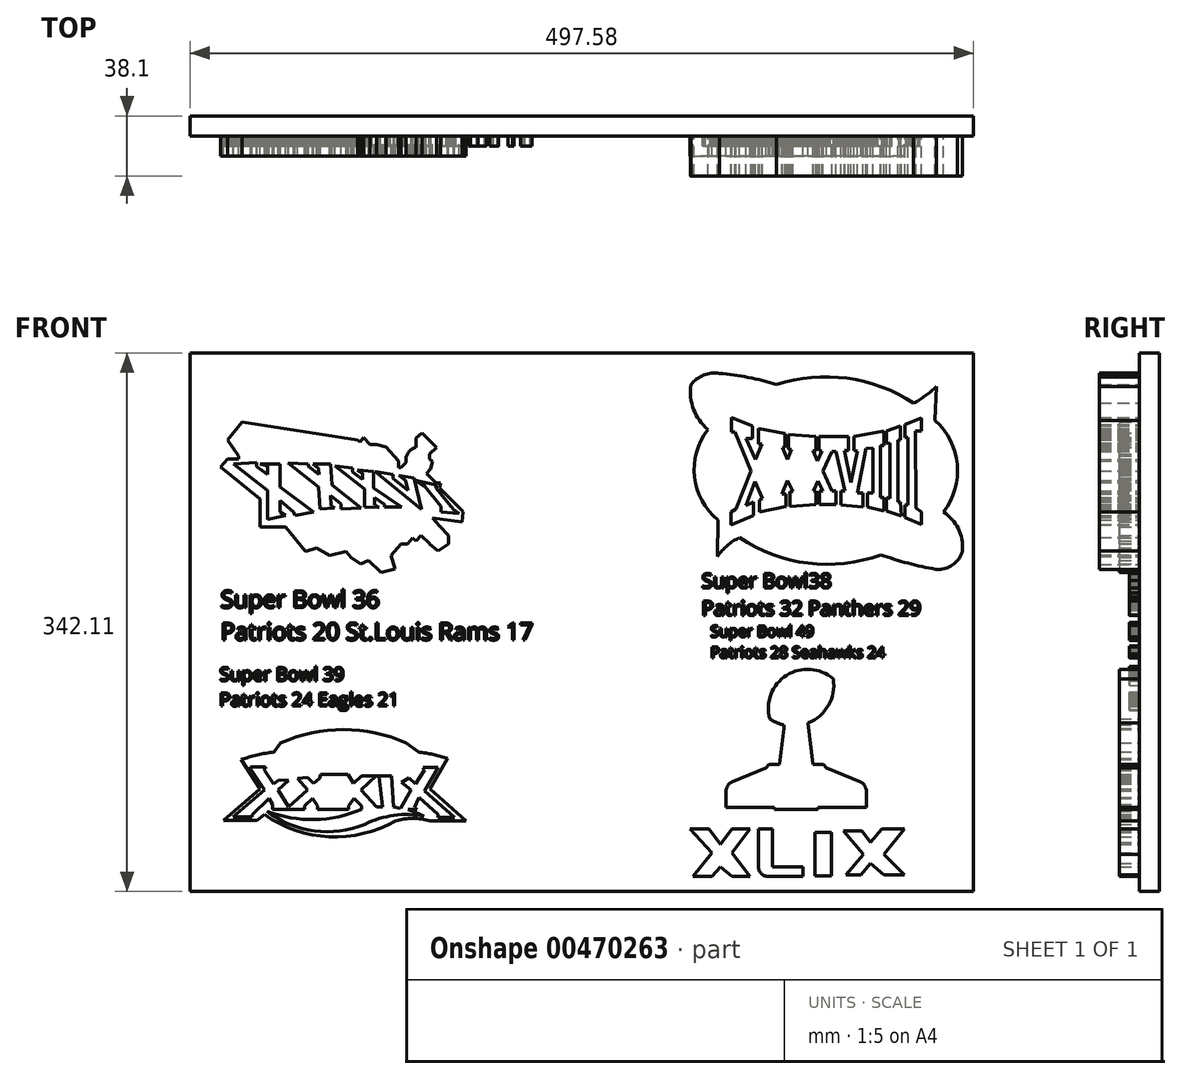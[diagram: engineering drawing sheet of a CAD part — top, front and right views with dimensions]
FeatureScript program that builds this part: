
annotation { "Feature Type Name" : "Feature", "Feature Type Description" : "" }
export const myFeature = defineFeature(function(context is Context, id is Id, definition is map)
    precondition{}
    {
        {
            var Q0;
            Q0=qCreatedBy(makeId("Front.planeOp"),FACE);
            var sketch = newSketch(context, id + "F0", { "sketchPlane" : qUnion([Q0])});
            skLineSegment(sketch, "E0.bottom", {"start": v(-44.55, 100.86) * mm, "end": v(453.03, 100.86) * mm});
            skLineSegment(sketch, "E0.top", {"start": v(-44.55, -241.25) * mm, "end": v(453.03, -241.25) * mm});
            skLineSegment(sketch, "E0.left", {"start": v(-44.55, 100.86) * mm, "end": v(-44.55, -241.25) * mm});
            skLineSegment(sketch, "E0.right", {"start": v(453.03, 100.86) * mm, "end": v(453.03, -241.25) * mm});
            skSolve(sketch);
        }
        {
            var Q0;
            Q0 = qSketchRegion(id + "F0", true);
            extrude(context, id + "F1", {"entities" : qUnion([Q0]), "depth" : 12.7 * mm});
        }
        {
            var Q0;
            Q0=makeQuery(id+"F1.opExtrude","CAP_FACE",FACE,{"disambiguationData":[OSD([sQuery(id+"F0.wireOp",EDGE,"E0.bottom"),sQuery(id+"F0.wireOp",EDGE,"E0.top"),sQuery(id+"F0.wireOp",EDGE,"E0.left"),sQuery(id+"F0.wireOp",EDGE,"E0.right")])],"isStart":false});
            var sketch = newSketch(context, id + "F2", { "sketchPlane" : qUnion([Q0])});
            skArc(sketch, "E1", {"start": v(289.89, 58.13) * mm, "mid": v(275.62, 26.24) * mm, "end": v(290.82, -5.22) * mm});
            skArc(sketch, "E2", {"start": v(415.04, 68.98) * mm, "mid": v(350.57, 85.37) * mm, "end": v(289.89, 58.13) * mm});
            skArc(sketch, "E3", {"start": v(428.71, -5.7) * mm, "mid": v(442.95, 26.22) * mm, "end": v(428.71, 58.13) * mm});
            skArc(sketch, "E4", {"start": v(304.5, -16.36) * mm, "mid": v(368.5, -33) * mm, "end": v(428.71, -5.7) * mm});
            skArc(sketch, "E5", {"start": v(304.5, -16.36) * mm, "mid": v(296.68, -21.46) * mm, "end": v(290.46, -28.4) * mm});
            skArc(sketch, "E6", {"start": v(415.04, 68.98) * mm, "mid": v(422.63, 73.85) * mm, "end": v(429.6, 79.58) * mm});
            skLineSegment(sketch, "E7", {"start": v(429.6, 79.58) * mm, "end": v(428.71, 58.13) * mm});
            skLineSegment(sketch, "E8", {"start": v(290.82, -5.22) * mm, "end": v(290.46, -28.4) * mm});
            skArc(sketch, "E9", {"start": v(273.65, 80.73) * mm, "mid": v(275.27, 65.1) * mm, "end": v(284.32, 52.25) * mm});
            skArc(sketch, "E10", {"start": v(291.58, 87.97) * mm, "mid": v(281.63, 86.8) * mm, "end": v(273.65, 80.73) * mm});
            skArc(sketch, "E11", {"start": v(327.86, 80.73) * mm, "mid": v(309.93, 85.41) * mm, "end": v(291.58, 87.97) * mm});
            skArc(sketch, "E12", {"start": v(446.06, -24.78) * mm, "mid": v(443.4, -10.76) * mm, "end": v(434, 0) * mm});
            skArc(sketch, "E13", {"start": v(429.16, -36.5) * mm, "mid": v(439.76, -33.75) * mm, "end": v(446.06, -24.78) * mm});
            skArc(sketch, "E14", {"start": v(394.14, -27.3) * mm, "mid": v(411.45, -32.67) * mm, "end": v(429.16, -36.5) * mm});
            skLineSegment(sketch, "E15", {"start": v(299.48, 59.78) * mm, "end": v(299.48, 50.73) * mm});
            skLineSegment(sketch, "E16", {"start": v(299.48, 50.73) * mm, "end": v(301.47, 50.73) * mm});
            skLineSegment(sketch, "E17", {"start": v(301.47, 50.73) * mm, "end": v(311.84, 26) * mm});
            skLineSegment(sketch, "E18", {"start": v(311.84, 26) * mm, "end": v(302.35, 1.93) * mm});
            skLineSegment(sketch, "E19", {"start": v(302.35, 1.93) * mm, "end": v(299.04, 0) * mm});
            skLineSegment(sketch, "E20", {"start": v(299.04, 0) * mm, "end": v(299.04, -8.45) * mm});
            skLineSegment(sketch, "E21", {"start": v(299.04, -8.45) * mm, "end": v(313.39, -2.49) * mm});
            skLineSegment(sketch, "E22", {"start": v(313.39, -2.49) * mm, "end": v(313.39, 6.12) * mm});
            skLineSegment(sketch, "E23", {"start": v(313.39, 6.12) * mm, "end": v(308.53, 4.14) * mm});
            skLineSegment(sketch, "E24", {"start": v(308.53, 4.14) * mm, "end": v(314.27, 19.15) * mm});
            skLineSegment(sketch, "E25", {"start": v(314.27, 19.15) * mm, "end": v(318.9, 8.33) * mm});
            skLineSegment(sketch, "E26", {"start": v(318.9, 8.33) * mm, "end": v(317.04, 7.53) * mm});
            skLineSegment(sketch, "E27", {"start": v(317.04, 7.53) * mm, "end": v(317.04, 0) * mm});
            skLineSegment(sketch, "E28", {"start": v(317.04, 0) * mm, "end": v(333.85, 3.41) * mm});
            skLineSegment(sketch, "E29", {"start": v(333.85, 3.41) * mm, "end": v(333.85, 11.28) * mm});
            skLineSegment(sketch, "E30", {"start": v(333.85, 11.28) * mm, "end": v(331.34, 11.28) * mm});
            skLineSegment(sketch, "E31", {"start": v(331.34, 11.28) * mm, "end": v(335.03, 19.99) * mm});
            skLineSegment(sketch, "E32", {"start": v(335.03, 19.99) * mm, "end": v(338.54, 12.79) * mm});
            skLineSegment(sketch, "E33", {"start": v(338.54, 12.79) * mm, "end": v(336.36, 12.79) * mm});
            skLineSegment(sketch, "E34", {"start": v(336.36, 12.79) * mm, "end": v(336.36, 3.41) * mm});
            skLineSegment(sketch, "E35", {"start": v(336.36, 3.41) * mm, "end": v(353.1, 4.75) * mm});
            skLineSegment(sketch, "E36", {"start": v(317.04, 26.85) * mm, "end": v(324.14, 9.14) * mm});
            skLineSegment(sketch, "E37", {"start": v(317.04, 26.85) * mm, "end": v(324.14, 41.96) * mm});
            skLineSegment(sketch, "E38", {"start": v(324.14, 41.96) * mm, "end": v(325.9, 41.96) * mm});
            skLineSegment(sketch, "E39", {"start": v(325.9, 41.96) * mm, "end": v(332.27, 26.45) * mm});
            skLineSegment(sketch, "E40", {"start": v(332.27, 26.45) * mm, "end": v(325.9, 9.57) * mm});
            skLineSegment(sketch, "E41", {"start": v(324.14, 9.14) * mm, "end": v(325.9, 9.57) * mm});
            skLineSegment(sketch, "E42", {"start": v(318.57, 43.21) * mm, "end": v(314.54, 33.27) * mm});
            skLineSegment(sketch, "E43", {"start": v(318.57, 43.21) * mm, "end": v(316.5, 43.21) * mm});
            skLineSegment(sketch, "E44", {"start": v(316.5, 43.21) * mm, "end": v(316.5, 53.05) * mm});
            skLineSegment(sketch, "E45", {"start": v(314.54, 33.27) * mm, "end": v(308.63, 46.63) * mm});
            skLineSegment(sketch, "E46", {"start": v(308.63, 46.63) * mm, "end": v(312.57, 46.63) * mm});
            skLineSegment(sketch, "E47", {"start": v(312.57, 46.63) * mm, "end": v(312.57, 54.6) * mm});
            skLineSegment(sketch, "E48", {"start": v(312.57, 54.6) * mm, "end": v(299.48, 59.78) * mm});
            skLineSegment(sketch, "E49", {"start": v(316.5, 53.05) * mm, "end": v(333.42, 49.68) * mm});
            skLineSegment(sketch, "E50", {"start": v(333.42, 49.68) * mm, "end": v(333.42, 40.97) * mm});
            skLineSegment(sketch, "E51", {"start": v(333.42, 40.97) * mm, "end": v(331.8, 40.97) * mm});
            skLineSegment(sketch, "E52", {"start": v(331.8, 40.97) * mm, "end": v(335.02, 33.27) * mm});
            skLineSegment(sketch, "E53", {"start": v(335.02, 33.27) * mm, "end": v(337.53, 39.44) * mm});
            skLineSegment(sketch, "E54", {"start": v(337.53, 39.44) * mm, "end": v(335.64, 39.44) * mm});
            skLineSegment(sketch, "E55", {"start": v(335.64, 39.44) * mm, "end": v(335.64, 49.17) * mm});
            skLineSegment(sketch, "E56", {"start": v(335.64, 49.17) * mm, "end": v(353.02, 47.75) * mm});
            skLineSegment(sketch, "E57", {"start": v(353.1, 4.75) * mm, "end": v(353.1, 13.17) * mm});
            skLineSegment(sketch, "E58", {"start": v(353.1, 13.17) * mm, "end": v(351.4, 13.17) * mm});
            skLineSegment(sketch, "E59", {"start": v(351.4, 13.17) * mm, "end": v(354.26, 19.44) * mm});
            skLineSegment(sketch, "E60", {"start": v(354.26, 19.44) * mm, "end": v(357.44, 13.17) * mm});
            skLineSegment(sketch, "E61", {"start": v(357.44, 13.17) * mm, "end": v(355.27, 13.17) * mm});
            skLineSegment(sketch, "E62", {"start": v(355.27, 13.17) * mm, "end": v(355.27, 4.75) * mm});
            skLineSegment(sketch, "E63", {"start": v(355.27, 4.75) * mm, "end": v(365.63, 4.75) * mm});
            skLineSegment(sketch, "E64", {"start": v(365.63, 4.66) * mm, "end": v(365.63, 13.17) * mm});
            skLineSegment(sketch, "E65", {"start": v(365.63, 13.17) * mm, "end": v(363.08, 13.17) * mm});
            skLineSegment(sketch, "E66", {"start": v(363.08, 13.17) * mm, "end": v(357.44, 25.8) * mm});
            skLineSegment(sketch, "E67", {"start": v(357.44, 25.8) * mm, "end": v(363.08, 38.15) * mm});
            skLineSegment(sketch, "E68", {"start": v(363.08, 38.15) * mm, "end": v(365.63, 38.15) * mm});
            skLineSegment(sketch, "E69", {"start": v(353.02, 47.75) * mm, "end": v(353.02, 38.63) * mm});
            skLineSegment(sketch, "E70", {"start": v(353.02, 38.63) * mm, "end": v(351.08, 38.79) * mm});
            skLineSegment(sketch, "E71", {"start": v(351.08, 38.79) * mm, "end": v(353.88, 32.1) * mm});
            skLineSegment(sketch, "E72", {"start": v(353.88, 32.1) * mm, "end": v(356.95, 38.63) * mm});
            skLineSegment(sketch, "E73", {"start": v(356.95, 38.63) * mm, "end": v(355.01, 38.79) * mm});
            skLineSegment(sketch, "E74", {"start": v(355.01, 38.79) * mm, "end": v(355.01, 47.75) * mm});
            skLineSegment(sketch, "E75", {"start": v(356.95, 47.75) * mm, "end": v(373.54, 47.75) * mm});
            skLineSegment(sketch, "E76", {"start": v(373.54, 47.75) * mm, "end": v(373.54, 38.79) * mm});
            skLineSegment(sketch, "E77", {"start": v(373.54, 38.79) * mm, "end": v(371.1, 38.99) * mm});
            skLineSegment(sketch, "E78", {"start": v(371.1, 38.99) * mm, "end": v(375.28, 18.71) * mm});
            skLineSegment(sketch, "E79", {"start": v(375.28, 18.71) * mm, "end": v(379.2, 38.63) * mm});
            skLineSegment(sketch, "E80", {"start": v(379.2, 38.63) * mm, "end": v(377.27, 38.79) * mm});
            skLineSegment(sketch, "E81", {"start": v(377.27, 38.79) * mm, "end": v(377.27, 47.75) * mm});
            skLineSegment(sketch, "E82", {"start": v(355.01, 47.75) * mm, "end": v(356.95, 47.75) * mm});
            skLineSegment(sketch, "E83", {"start": v(343.5, 12.78) * mm, "end": v(346.08, 12.78) * mm});
            skLineSegment(sketch, "E84", {"start": v(346.08, 12.78) * mm, "end": v(352.05, 25.84) * mm});
            skLineSegment(sketch, "E85", {"start": v(352.05, 25.84) * mm, "end": v(346.08, 38.7) * mm});
            skLineSegment(sketch, "E86", {"start": v(346.08, 38.7) * mm, "end": v(343.38, 38.7) * mm});
            skLineSegment(sketch, "E87", {"start": v(343.38, 38.7) * mm, "end": v(337.5, 25.84) * mm});
            skLineSegment(sketch, "E88", {"start": v(337.5, 25.84) * mm, "end": v(343.5, 12.78) * mm});
            skLineSegment(sketch, "E89", {"start": v(365.63, 38.15) * mm, "end": v(371.36, 13.21) * mm});
            skLineSegment(sketch, "E90", {"start": v(371.36, 13.21) * mm, "end": v(368.86, 13.21) * mm});
            skLineSegment(sketch, "E91", {"start": v(368.86, 13.21) * mm, "end": v(368.86, 4.17) * mm});
            skLineSegment(sketch, "E92", {"start": v(368.86, 4.17) * mm, "end": v(382.76, 3.06) * mm});
            skLineSegment(sketch, "E93", {"start": v(382.76, 3.06) * mm, "end": v(382.76, 11.82) * mm});
            skLineSegment(sketch, "E94", {"start": v(382.76, 11.82) * mm, "end": v(379.43, 11.82) * mm});
            skLineSegment(sketch, "E95", {"start": v(379.43, 11.82) * mm, "end": v(384.71, 40.06) * mm});
            skLineSegment(sketch, "E96", {"start": v(384.71, 40.06) * mm, "end": v(389.16, 40.47) * mm});
            skLineSegment(sketch, "E97", {"start": v(389.16, 40.47) * mm, "end": v(389.16, 11.82) * mm});
            skLineSegment(sketch, "E98", {"start": v(389.16, 11.82) * mm, "end": v(385.69, 11.82) * mm});
            skLineSegment(sketch, "E99", {"start": v(385.69, 11.82) * mm, "end": v(385.69, 3.06) * mm});
            skLineSegment(sketch, "E100", {"start": v(385.69, 3.06) * mm, "end": v(396.26, 0.42) * mm});
            skLineSegment(sketch, "E101", {"start": v(396.26, 0.42) * mm, "end": v(396.26, 9.04) * mm});
            skLineSegment(sketch, "E102", {"start": v(396.26, 9.04) * mm, "end": v(394.03, 9.04) * mm});
            skLineSegment(sketch, "E103", {"start": v(394.03, 9.04) * mm, "end": v(394.03, 42) * mm});
            skLineSegment(sketch, "E104", {"start": v(394.03, 42) * mm, "end": v(396.12, 42) * mm});
            skLineSegment(sketch, "E105", {"start": v(396.12, 42) * mm, "end": v(396.12, 51.46) * mm});
            skLineSegment(sketch, "E106", {"start": v(396.12, 51.46) * mm, "end": v(377.27, 47.75) * mm});
            skLineSegment(sketch, "E107", {"start": v(397.84, 51.46) * mm, "end": v(397.84, 43.46) * mm});
            skLineSegment(sketch, "E108", {"start": v(397.84, 43.46) * mm, "end": v(399.89, 43.65) * mm});
            skLineSegment(sketch, "E109", {"start": v(399.89, 43.65) * mm, "end": v(399.89, 8.6) * mm});
            skLineSegment(sketch, "E110", {"start": v(399.89, 8.6) * mm, "end": v(397.84, 9.04) * mm});
            skLineSegment(sketch, "E111", {"start": v(397.84, 9.04) * mm, "end": v(397.84, 0.42) * mm});
            skLineSegment(sketch, "E112", {"start": v(397.84, 0.42) * mm, "end": v(407.35, -2.58) * mm});
            skLineSegment(sketch, "E113", {"start": v(407.35, -2.58) * mm, "end": v(406.51, 6.3) * mm});
            skLineSegment(sketch, "E114", {"start": v(406.51, 6.3) * mm, "end": v(405, 6.15) * mm});
            skLineSegment(sketch, "E115", {"start": v(405, 6.15) * mm, "end": v(405, 45.5) * mm});
            skLineSegment(sketch, "E116", {"start": v(405, 45.5) * mm, "end": v(406.51, 45.65) * mm});
            skLineSegment(sketch, "E117", {"start": v(406.51, 45.65) * mm, "end": v(406.51, 54.6) * mm});
            skLineSegment(sketch, "E118", {"start": v(406.51, 54.6) * mm, "end": v(397.84, 51.46) * mm});
            skLineSegment(sketch, "E119", {"start": v(409.62, 47.3) * mm, "end": v(409.62, 55.37) * mm});
            skLineSegment(sketch, "E120", {"start": v(409.62, 47.3) * mm, "end": v(411.5, 47.3) * mm});
            skLineSegment(sketch, "E121", {"start": v(411.5, 47.3) * mm, "end": v(411.5, 4.35) * mm});
            skLineSegment(sketch, "E122", {"start": v(411.5, 4.35) * mm, "end": v(409.62, 4.35) * mm});
            skLineSegment(sketch, "E123", {"start": v(409.62, 4.35) * mm, "end": v(409.62, -3.56) * mm});
            skLineSegment(sketch, "E124", {"start": v(409.62, -3.56) * mm, "end": v(420, -7.9) * mm});
            skLineSegment(sketch, "E125", {"start": v(420, -7.9) * mm, "end": v(420, 0) * mm});
            skLineSegment(sketch, "E126", {"start": v(420, 0) * mm, "end": v(416.46, 2.38) * mm});
            skLineSegment(sketch, "E127", {"start": v(416.06, 51.33) * mm, "end": v(416.46, 2.38) * mm});
            skPoint(sketch, "E127.startSnap0", {"position": v(409.62, 51.33) * mm});
            skLineSegment(sketch, "E128", {"start": v(416.06, 51.33) * mm, "end": v(420, 51.37) * mm});
            skLineSegment(sketch, "E129", {"start": v(420, 51.37) * mm, "end": v(419.92, 59.7) * mm});
            skLineSegment(sketch, "E130", {"start": v(419.92, 59.7) * mm, "end": v(409.62, 55.37) * mm});
            skSolve(sketch);
        }
        {
            var Q0;
            Q0 = qSketchRegion(id + "F2", true);
            extrude(context, id + "F3", {"entities" : qUnion([Q0]), "operationType" : NewBodyOperationType.ADD, "depth" : 25.4 * mm});
        }
        {
            var Q0;
            {var subQ0=sQuery(id+"F0.wireOp",EDGE,"E0.left");var subQ1=sQuery(id+"F0.wireOp",EDGE,"E0.bottom");var subQ2=sQuery(id+"F0.wireOp",EDGE,"E0.right");var subQ3=sQuery(id+"F0.wireOp",EDGE,"E0.top");Q0=makeQuery(id+"F3.boolean.opBoolean","SPLIT",FACE,{"disambiguationData":[TD([makeQuery(id+"F1.opExtrude","SWEPT_FACE",FACE,{"disambiguationData":[OSD([subQ1])]})])],"derivedFrom":makeQuery(id+"F1.opExtrude","CAP_FACE",FACE,{"disambiguationData":[OSD([subQ1,subQ3,subQ0,subQ2])],"isStart":false})});}
            var sketch = newSketch(context, id + "F4", { "sketchPlane" : qUnion([Q0])});
            skLineSegment(sketch, "E131", {"start": v(326.56, -189.04) * mm, "end": v(347.97, -189.04) * mm});
            skLineSegment(sketch, "E132", {"start": v(347.97, -189.04) * mm, "end": v(344.69, -135.26) * mm});
            skLineSegment(sketch, "E133", {"start": v(348.03, -134.17) * mm, "end": v(354.36, -189.04) * mm});
            skLineSegment(sketch, "E134", {"start": v(354.36, -189.04) * mm, "end": v(347.97, -189.04) * mm});
            skLineSegment(sketch, "E135", {"start": v(326.56, -189.04) * mm, "end": v(332.51, -137.46) * mm});
            skPoint(sketch, "E136.orphan", {"position": v(344.6, -133.69) * mm});
            skArc(sketch, "E137", {"start": v(363.98, -106.14) * mm, "mid": v(334.37, -103.83) * mm, "end": v(323.67, -131.54) * mm});
            skArc(sketch, "E138", {"start": v(323.67, -131.54) * mm, "mid": v(352.16, -132.06) * mm, "end": v(363.98, -106.14) * mm});
            skLineSegment(sketch, "E139", {"start": v(332.51, -137.46) * mm, "end": v(332.51, -135.4) * mm});
            skPoint(sketch, "E140.orphan", {"position": v(347.97, -133.69) * mm});
            skLineSegment(sketch, "E141", {"start": v(272.83, -201.33) * mm, "end": v(284.99, -201.33) * mm});
            skLineSegment(sketch, "E142", {"start": v(284.99, -201.33) * mm, "end": v(292.35, -211.27) * mm});
            skLineSegment(sketch, "E143", {"start": v(292.35, -211.27) * mm, "end": v(299.72, -201.33) * mm});
            skLineSegment(sketch, "E144", {"start": v(299.72, -201.33) * mm, "end": v(311.14, -201.33) * mm});
            skLineSegment(sketch, "E145", {"start": v(311.14, -201.33) * mm, "end": v(299.72, -216.8) * mm});
            skLineSegment(sketch, "E146", {"start": v(299.72, -216.8) * mm, "end": v(311.14, -231.66) * mm});
            skLineSegment(sketch, "E147", {"start": v(311.14, -231.66) * mm, "end": v(299.72, -231.66) * mm});
            skLineSegment(sketch, "E148", {"start": v(299.72, -231.66) * mm, "end": v(292.35, -225.4) * mm});
            skLineSegment(sketch, "E149", {"start": v(292.35, -225.4) * mm, "end": v(287.03, -231.66) * mm});
            skLineSegment(sketch, "E150", {"start": v(287.03, -231.66) * mm, "end": v(275, -231.66) * mm});
            skLineSegment(sketch, "E151", {"start": v(275, -231.66) * mm, "end": v(287.03, -216.8) * mm});
            skLineSegment(sketch, "E152", {"start": v(287.03, -216.8) * mm, "end": v(272.83, -201.33) * mm});
            skLineSegment(sketch, "E153", {"start": v(316.45, -201.33) * mm, "end": v(316.45, -225.3) * mm});
            skLineSegment(sketch, "E154", {"start": v(322.8, -231.66) * mm, "end": v(344.65, -231.66) * mm});
            skLineSegment(sketch, "E155", {"start": v(344.65, -231.66) * mm, "end": v(344.65, -225.4) * mm});
            skLineSegment(sketch, "E156", {"start": v(344.65, -225.4) * mm, "end": v(325.5, -225.4) * mm});
            skLineSegment(sketch, "E157", {"start": v(325.5, -225.4) * mm, "end": v(325.5, -201.33) * mm});
            skLineSegment(sketch, "E158", {"start": v(325.5, -201.33) * mm, "end": v(316.45, -201.33) * mm});
            skLineSegment(sketch, "E159.bottom", {"start": v(352.39, -203.54) * mm, "end": v(362.7, -203.54) * mm});
            skLineSegment(sketch, "E159.top", {"start": v(352.39, -231.16) * mm, "end": v(362.7, -231.16) * mm});
            skLineSegment(sketch, "E159.left", {"start": v(352.39, -203.54) * mm, "end": v(352.39, -231.16) * mm});
            skLineSegment(sketch, "E159.right", {"start": v(362.7, -203.54) * mm, "end": v(362.7, -231.16) * mm});
            skPoint(sketch, "E160.visualSharp", {"position": v(316.45, -231.66) * mm});
            skArc(sketch, "E160.filletArc", {"start": v(316.45, -225.3) * mm, "mid": v(318.31, -229.8) * mm, "end": v(322.8, -231.66) * mm});
            skLineSegment(sketch, "E161", {"start": v(370.43, -202.54) * mm, "end": v(382.27, -202.54) * mm});
            skLineSegment(sketch, "E162", {"start": v(394.96, -201.47) * mm, "end": v(409.26, -201.47) * mm});
            skLineSegment(sketch, "E163", {"start": v(409.26, -201.47) * mm, "end": v(396.24, -217.45) * mm});
            skLineSegment(sketch, "E164", {"start": v(396.24, -217.45) * mm, "end": v(409.26, -230.48) * mm});
            skLineSegment(sketch, "E165", {"start": v(409.26, -230.48) * mm, "end": v(396.24, -230.48) * mm});
            skLineSegment(sketch, "E166", {"start": v(396.24, -230.48) * mm, "end": v(387.62, -223.25) * mm});
            skLineSegment(sketch, "E167", {"start": v(387.62, -223.25) * mm, "end": v(381.56, -230.48) * mm});
            skLineSegment(sketch, "E168", {"start": v(381.56, -230.48) * mm, "end": v(372.09, -230.48) * mm});
            skLineSegment(sketch, "E169", {"start": v(372.09, -230.48) * mm, "end": v(383.22, -217.45) * mm});
            skLineSegment(sketch, "E170", {"start": v(383.22, -217.45) * mm, "end": v(370.43, -202.54) * mm});
            skLineSegment(sketch, "E171", {"start": v(382.27, -202.54) * mm, "end": v(387.62, -209.99) * mm});
            skLineSegment(sketch, "E172", {"start": v(387.62, -209.99) * mm, "end": v(394.96, -201.47) * mm});
            skLineSegment(sketch, "E173", {"start": v(295.92, -187.74) * mm, "end": v(295.92, -177.52) * mm});
            skLineSegment(sketch, "E174", {"start": v(299.8, -171.67) * mm, "end": v(321.26, -162.66) * mm});
            skLineSegment(sketch, "E175", {"start": v(321.26, -162.66) * mm, "end": v(323.03, -160.38) * mm});
            skLineSegment(sketch, "E176", {"start": v(323.03, -160.38) * mm, "end": v(329.87, -160.38) * mm});
            skLineSegment(sketch, "E177", {"start": v(295.92, -187.74) * mm, "end": v(326.7, -187.74) * mm});
            skPoint(sketch, "E178.visualSharp", {"position": v(295.92, -173.3) * mm});
            skArc(sketch, "E178.filletArc", {"start": v(299.8, -171.67) * mm, "mid": v(296.98, -174) * mm, "end": v(295.92, -177.52) * mm});
            skLineSegment(sketch, "E179", {"start": v(340.46, -189.04) * mm, "end": v(340.46, -130.63) * mm, "construction": true});
            skLineSegment(sketch, "E180.MirrorCS", {"start": v(357.9, -160.38) * mm, "end": v(351.05, -160.38) * mm});
            skLineSegment(sketch, "E181.MirrorCS", {"start": v(381.11, -171.67) * mm, "end": v(359.67, -162.66) * mm});
            skLineSegment(sketch, "E182.MirrorCS", {"start": v(359.67, -162.66) * mm, "end": v(357.9, -160.38) * mm});
            skArc(sketch, "E183.MirrorCS", {"start": v(381.11, -171.67) * mm, "mid": v(383.94, -174) * mm, "end": v(385, -177.52) * mm});
            skLineSegment(sketch, "E184.MirrorCS", {"start": v(385, -187.74) * mm, "end": v(385, -177.52) * mm});
            skLineSegment(sketch, "E185.MirrorCS", {"start": v(385, -187.74) * mm, "end": v(354.21, -187.74) * mm});
            skSolve(sketch);
        }
        {
            var Q0;
            Q0 = qSketchRegion(id + "F4", true);
            extrude(context, id + "F5", {"entities" : qUnion([Q0]), "operationType" : NewBodyOperationType.ADD, "depth" : 12.7 * mm});
        }
        {
            var Q0;
            {var subQ0=sQuery(id+"F0.wireOp",EDGE,"E0.left");var subQ1=sQuery(id+"F0.wireOp",EDGE,"E0.bottom");var subQ2=sQuery(id+"F0.wireOp",EDGE,"E0.right");var subQ3=sQuery(id+"F0.wireOp",EDGE,"E0.top");Q0=makeQuery(id+"F3.boolean.opBoolean","SPLIT",FACE,{"disambiguationData":[TD([makeQuery(id+"F1.opExtrude","SWEPT_FACE",FACE,{"disambiguationData":[OSD([subQ1])]})])],"derivedFrom":makeQuery(id+"F1.opExtrude","CAP_FACE",FACE,{"disambiguationData":[OSD([subQ1,subQ3,subQ0,subQ2])],"isStart":false})});}
            var sketch = newSketch(context, id + "F6", { "sketchPlane" : qUnion([Q0])});
            skLineSegment(sketch, "E186", {"start": v(8.94, -152.54) * mm, "end": v(13.1, -146.72) * mm});
            skLineSegment(sketch, "E187", {"start": v(92.67, -146.72) * mm, "end": v(100.5, -152.54) * mm});
            skArc(sketch, "E188", {"start": v(92.67, -146.72) * mm, "mid": v(52.88, -138.38) * mm, "end": v(13.1, -146.72) * mm});
            skArc(sketch, "E189", {"start": v(8.94, -152.54) * mm, "mid": v(-1.74, -154.47) * mm, "end": v(-12.18, -157.42) * mm});
            skArc(sketch, "E190.MirrorCS", {"start": v(100.5, -152.54) * mm, "mid": v(109.85, -154.18) * mm, "end": v(119.03, -156.6) * mm});
            skLineSegment(sketch, "E191", {"start": v(119.03, -156.6) * mm, "end": v(107.85, -175.9) * mm});
            skLineSegment(sketch, "E192", {"start": v(107.85, -175.9) * mm, "end": v(130.84, -196.28) * mm});
            skLineSegment(sketch, "E193", {"start": v(130.84, -196.28) * mm, "end": v(107.85, -196.28) * mm});
            skArc(sketch, "E194", {"start": v(107.85, -196.28) * mm, "mid": v(97, -194.75) * mm, "end": v(86.15, -196.28) * mm});
            skArc(sketch, "E195", {"start": v(2.65, -192.28) * mm, "mid": v(43.82, -206.36) * mm, "end": v(86.15, -196.28) * mm});
            skLineSegment(sketch, "E196", {"start": v(-12.18, -157.42) * mm, "end": v(0, -175.95) * mm});
            skLineSegment(sketch, "E197", {"start": v(0, -175.95) * mm, "end": v(-23.3, -196.17) * mm});
            skLineSegment(sketch, "E198", {"start": v(-23.3, -196.17) * mm, "end": v(-1.96, -196.17) * mm});
            skLineSegment(sketch, "E199", {"start": v(-1.96, -196.17) * mm, "end": v(2.65, -192.28) * mm});
            skLineSegment(sketch, "E200", {"start": v(-6.09, -163.29) * mm, "end": v(2.65, -176.58) * mm});
            skPoint(sketch, "E200.startSnap0", {"position": v(-6.09, -166.69) * mm});
            skLineSegment(sketch, "E201", {"start": v(2.65, -176.58) * mm, "end": v(-17.17, -193.78) * mm});
            skLineSegment(sketch, "E202", {"start": v(-17.17, -193.78) * mm, "end": v(-5.3, -193.78) * mm});
            skLineSegment(sketch, "E203", {"start": v(-5.3, -193.78) * mm, "end": v(-5.3, -192.55) * mm});
            skLineSegment(sketch, "E204", {"start": v(-5.3, -192.55) * mm, "end": v(5.77, -182.03) * mm});
            skLineSegment(sketch, "E205", {"start": v(5.77, -182.03) * mm, "end": v(7.94, -185.8) * mm});
            skLineSegment(sketch, "E206", {"start": v(7.94, -185.8) * mm, "end": v(7.94, -189) * mm});
            skLineSegment(sketch, "E207", {"start": v(7.94, -189) * mm, "end": v(28.06, -189) * mm});
            skLineSegment(sketch, "E208", {"start": v(28.06, -189) * mm, "end": v(28.06, -186.83) * mm});
            skLineSegment(sketch, "E209", {"start": v(28.06, -186.83) * mm, "end": v(33.21, -182.03) * mm});
            skLineSegment(sketch, "E210", {"start": v(33.21, -182.03) * mm, "end": v(36.3, -186.83) * mm});
            skLineSegment(sketch, "E211", {"start": v(36.3, -186.83) * mm, "end": v(36.3, -189) * mm});
            skLineSegment(sketch, "E212", {"start": v(36.3, -189) * mm, "end": v(56.2, -189) * mm});
            skLineSegment(sketch, "E213", {"start": v(56.2, -189) * mm, "end": v(56.2, -186.83) * mm});
            skLineSegment(sketch, "E214", {"start": v(56.2, -186.83) * mm, "end": v(59.74, -182.03) * mm});
            skLineSegment(sketch, "E215", {"start": v(59.74, -182.03) * mm, "end": v(64.31, -186.83) * mm});
            skLineSegment(sketch, "E216", {"start": v(64.28, -167.76) * mm, "end": v(73.66, -167.76) * mm});
            skLineSegment(sketch, "E217", {"start": v(73.66, -167.76) * mm, "end": v(64.2, -176.66) * mm});
            skLineSegment(sketch, "E218", {"start": v(64.2, -176.66) * mm, "end": v(73.8, -187.4) * mm});
            skLineSegment(sketch, "E219", {"start": v(73.8, -187.4) * mm, "end": v(77.7, -187.4) * mm});
            skLineSegment(sketch, "E220", {"start": v(77.7, -187.4) * mm, "end": v(75.4, -167.97) * mm});
            skLineSegment(sketch, "E221", {"start": v(75.4, -167.97) * mm, "end": v(73.8, -167.76) * mm});
            skLineSegment(sketch, "E222", {"start": v(73.8, -167.76) * mm, "end": v(83.38, -167.76) * mm});
            skLineSegment(sketch, "E223", {"start": v(83.38, -167.76) * mm, "end": v(84.78, -187.4) * mm});
            skLineSegment(sketch, "E224", {"start": v(84.78, -187.4) * mm, "end": v(89.13, -188.32) * mm});
            skLineSegment(sketch, "E225", {"start": v(89.13, -188.32) * mm, "end": v(95.76, -176.66) * mm});
            skLineSegment(sketch, "E226", {"start": v(95.76, -176.66) * mm, "end": v(89.93, -171.74) * mm});
            skLineSegment(sketch, "E227", {"start": v(89.93, -171.74) * mm, "end": v(94.39, -168.88) * mm});
            skLineSegment(sketch, "E228", {"start": v(94.39, -168.88) * mm, "end": v(98.85, -172.88) * mm});
            skLineSegment(sketch, "E229", {"start": v(98.85, -172.88) * mm, "end": v(104.33, -163.87) * mm});
            skLineSegment(sketch, "E230", {"start": v(104.33, -163.87) * mm, "end": v(103.35, -162.44) * mm});
            skLineSegment(sketch, "E231", {"start": v(103.35, -162.44) * mm, "end": v(112.82, -162.44) * mm});
            skLineSegment(sketch, "E232", {"start": v(112.82, -162.44) * mm, "end": v(104.33, -177.15) * mm});
            skLineSegment(sketch, "E233", {"start": v(104.33, -177.15) * mm, "end": v(114.4, -186.09) * mm});
            skPoint(sketch, "E233.endSnap0", {"position": v(119.35, -186.09) * mm});
            skLineSegment(sketch, "E234", {"start": v(114.4, -186.09) * mm, "end": v(123.46, -194.12) * mm});
            skLineSegment(sketch, "E235", {"start": v(123.46, -194.12) * mm, "end": v(113.08, -194.12) * mm});
            skLineSegment(sketch, "E236", {"start": v(113.08, -194.12) * mm, "end": v(113.08, -192.3) * mm});
            skLineSegment(sketch, "E237", {"start": v(113.08, -192.3) * mm, "end": v(100.85, -181.46) * mm});
            skLineSegment(sketch, "E238", {"start": v(100.85, -181.46) * mm, "end": v(99.26, -184.98) * mm});
            skLineSegment(sketch, "E239", {"start": v(99.26, -184.98) * mm, "end": v(98.03, -187.77) * mm});
            skLineSegment(sketch, "E240", {"start": v(98.03, -187.77) * mm, "end": v(99.53, -189.1) * mm});
            skLineSegment(sketch, "E241", {"start": v(99.53, -189.1) * mm, "end": v(94, -189.1) * mm});
            skArc(sketch, "E242", {"start": v(104.21, -193.44) * mm, "mid": v(99.14, -191.2) * mm, "end": v(94, -189.1) * mm});
            skArc(sketch, "E243", {"start": v(4.28, -190.25) * mm, "mid": v(34.47, -195.46) * mm, "end": v(64.4, -189) * mm});
            skArc(sketch, "E244", {"start": v(4.28, -190.25) * mm, "mid": v(34.35, -202.71) * mm, "end": v(66.62, -198.47) * mm});
            skArc(sketch, "E245", {"start": v(104.21, -193.44) * mm, "mid": v(85, -192.82) * mm, "end": v(66.62, -198.47) * mm});
            skLineSegment(sketch, "E246", {"start": v(64.31, -186.83) * mm, "end": v(64.4, -189) * mm});
            skLineSegment(sketch, "E247", {"start": v(11.3, -176.58) * mm, "end": v(18, -187.4) * mm});
            skPoint(sketch, "E247.endSnap0", {"position": v(18, -189) * mm});
            skLineSegment(sketch, "E248", {"start": v(18, -187.4) * mm, "end": v(30.12, -176.58) * mm});
            skLineSegment(sketch, "E249", {"start": v(30.12, -176.58) * mm, "end": v(23.67, -169.36) * mm});
            skLineSegment(sketch, "E250", {"start": v(11.3, -176.58) * mm, "end": v(18, -170.6) * mm});
            skLineSegment(sketch, "E251", {"start": v(23.67, -169.36) * mm, "end": v(30.12, -168.6) * mm});
            skLineSegment(sketch, "E252", {"start": v(30.12, -168.6) * mm, "end": v(33.94, -172.66) * mm});
            skLineSegment(sketch, "E253", {"start": v(33.94, -172.66) * mm, "end": v(37.64, -169.36) * mm});
            skLineSegment(sketch, "E254", {"start": v(38.17, -168.43) * mm, "end": v(38.24, -166.93) * mm});
            skLineSegment(sketch, "E255", {"start": v(38.24, -166.93) * mm, "end": v(55.71, -166.93) * mm});
            skLineSegment(sketch, "E256", {"start": v(55.71, -166.93) * mm, "end": v(59.37, -172.5) * mm});
            skLineSegment(sketch, "E257", {"start": v(59.37, -172.5) * mm, "end": v(64.28, -167.76) * mm});
            skLineSegment(sketch, "E258", {"start": v(-6.09, -163.29) * mm, "end": v(-6.09, -162.02) * mm});
            skLineSegment(sketch, "E259", {"start": v(-6.16, -162.02) * mm, "end": v(3.45, -162.02) * mm});
            skLineSegment(sketch, "E260", {"start": v(3.45, -161.97) * mm, "end": v(3.45, -163.05) * mm});
            skLineSegment(sketch, "E261", {"start": v(3.47, -163.05) * mm, "end": v(2.73, -163.05) * mm});
            skLineSegment(sketch, "E262", {"start": v(2.73, -163.02) * mm, "end": v(2.73, -164.15) * mm});
            skLineSegment(sketch, "E263", {"start": v(2.73, -164.15) * mm, "end": v(8.44, -172.83) * mm});
            skLineSegment(sketch, "E264", {"start": v(8.44, -172.83) * mm, "end": v(12.08, -170.44) * mm});
            skLineSegment(sketch, "E265", {"start": v(12.08, -170.44) * mm, "end": v(18, -170.6) * mm});
            skPoint(sketch, "E266.startSnap0", {"position": v(46.98, -166.93) * mm});
            skLineSegment(sketch, "E267", {"start": v(38.17, -168.43) * mm, "end": v(37.64, -169.36) * mm});
            skPoint(sketch, "E268.orphan", {"position": v(121.61, -157.42) * mm});
            skLineSegment(sketch, "E269", {"start": v(46.98, -166.93) * mm, "end": v(37.7, -177.18) * mm});
            skLineSegment(sketch, "E270", {"start": v(37.7, -177.18) * mm, "end": v(46.25, -189) * mm});
            skSolve(sketch);
        }
        {
            var Q0;
            Q0 = qSketchRegion(id + "F6", true);
            extrude(context, id + "F7", {"entities" : qUnion([Q0]), "operationType" : NewBodyOperationType.ADD, "depth" : 12.7 * mm});
        }
        {
            var Q0;
            {var subQ5=sQuery(id+"F0.wireOp",EDGE,"E0.left");var subQ7=sQuery(id+"F0.wireOp",EDGE,"E0.bottom");var subQ8=makeQuery(id+"F1.opExtrude","SWEPT_FACE",FACE,{"disambiguationData":[OSD([subQ7])]});var subQ10=sQuery(id+"F0.wireOp",EDGE,"E0.right");var subQ13=sQuery(id+"F0.wireOp",EDGE,"E0.top");Q0=makeQuery(id+"F7.boolean.opBoolean","SPLIT",FACE,{"disambiguationData":[TD([subQ8])],"derivedFrom":makeQuery(id+"F3.boolean.opBoolean","SPLIT",FACE,{"disambiguationData":[TD([subQ8])],"derivedFrom":makeQuery(id+"F1.opExtrude","CAP_FACE",FACE,{"disambiguationData":[OSD([subQ7,subQ13,subQ5,subQ10])],"isStart":false})})});}
            var sketch = newSketch(context, id + "F8", { "sketchPlane" : qUnion([Q0])});
            skLineSegment(sketch, "E271", {"start": v(-20.85, 25.06) * mm, "end": v(0, 8.2) * mm});
            skLineSegment(sketch, "E272", {"start": v(0, 8.2) * mm, "end": v(0, -9.8) * mm});
            skLineSegment(sketch, "E273", {"start": v(0, -9.8) * mm, "end": v(16.02, -9.8) * mm});
            skLineSegment(sketch, "E274", {"start": v(16.02, -9.8) * mm, "end": v(28.88, -25.24) * mm});
            skLineSegment(sketch, "E275", {"start": v(28.88, -25.24) * mm, "end": v(35.74, -22.95) * mm});
            skLineSegment(sketch, "E276", {"start": v(35.74, -22.95) * mm, "end": v(44.03, -27.8) * mm});
            skLineSegment(sketch, "E277", {"start": v(44.03, -27.8) * mm, "end": v(54.6, -25.24) * mm});
            skLineSegment(sketch, "E278", {"start": v(54.6, -25.24) * mm, "end": v(57.74, -28.95) * mm});
            skLineSegment(sketch, "E279", {"start": v(57.74, -28.95) * mm, "end": v(63.75, -33.24) * mm});
            skLineSegment(sketch, "E280", {"start": v(63.75, -33.24) * mm, "end": v(68.9, -30.95) * mm});
            skLineSegment(sketch, "E281", {"start": v(68.9, -30.95) * mm, "end": v(76.9, -38.67) * mm});
            skLineSegment(sketch, "E282", {"start": v(76.9, -38.67) * mm, "end": v(85.75, -36.38) * mm});
            skLineSegment(sketch, "E283", {"start": v(89.43, -20.3) * mm, "end": v(83.18, -27.8) * mm});
            skLineSegment(sketch, "E284", {"start": v(83.18, -27.8) * mm, "end": v(85.75, -36.38) * mm});
            skLineSegment(sketch, "E285", {"start": v(89.43, -20.3) * mm, "end": v(93.5, -20.3) * mm});
            skLineSegment(sketch, "E286", {"start": v(93.5, -20.3) * mm, "end": v(96.9, -16.66) * mm});
            skLineSegment(sketch, "E287", {"start": v(96.9, -16.66) * mm, "end": v(98.87, -18.5) * mm});
            skLineSegment(sketch, "E288", {"start": v(98.87, -18.5) * mm, "end": v(102.12, -15.02) * mm});
            skLineSegment(sketch, "E289", {"start": v(102.12, -15.02) * mm, "end": v(107.5, -20.04) * mm});
            skLineSegment(sketch, "E290", {"start": v(107.5, -20.04) * mm, "end": v(107.5, -20.3) * mm});
            skLineSegment(sketch, "E291", {"start": v(107.5, -20.3) * mm, "end": v(112.89, -24.8) * mm});
            skLineSegment(sketch, "E292", {"start": v(112.89, -24.8) * mm, "end": v(119.48, -20.3) * mm});
            skLineSegment(sketch, "E293", {"start": v(119.48, -20.3) * mm, "end": v(119.48, -15.02) * mm});
            skLineSegment(sketch, "E294", {"start": v(119.48, -15.02) * mm, "end": v(113.95, -9.04) * mm});
            skLineSegment(sketch, "E295", {"start": v(109.35, -4.07) * mm, "end": v(113.95, -9.04) * mm});
            skLineSegment(sketch, "E296", {"start": v(109.35, -4.07) * mm, "end": v(128.08, -6.56) * mm});
            skPoint(sketch, "E296.endSnap0", {"position": v(111.65, -6.56) * mm});
            skLineSegment(sketch, "E297", {"start": v(128.08, -6.56) * mm, "end": v(128.95, 0) * mm});
            skLineSegment(sketch, "E298", {"start": v(128.24, 0.67) * mm, "end": v(113.95, 14.96) * mm});
            skLineSegment(sketch, "E299", {"start": v(113.95, 14.96) * mm, "end": v(114.4, 18.42) * mm});
            skLineSegment(sketch, "E300", {"start": v(114.4, 18.42) * mm, "end": v(111.7, 18.42) * mm});
            skLineSegment(sketch, "E301", {"start": v(111.7, 18.42) * mm, "end": v(105.75, 24.38) * mm});
            skLineSegment(sketch, "E302", {"start": v(105.75, 24.38) * mm, "end": v(108.3, 27.03) * mm});
            skLineSegment(sketch, "E303", {"start": v(108.3, 27.03) * mm, "end": v(109.35, 31.84) * mm});
            skLineSegment(sketch, "E304", {"start": v(109.35, 31.84) * mm, "end": v(107.62, 33.56) * mm});
            skLineSegment(sketch, "E305", {"start": v(107.62, 33.56) * mm, "end": v(107.62, 36.74) * mm});
            skLineSegment(sketch, "E306", {"start": v(107.62, 36.74) * mm, "end": v(111.87, 40.99) * mm});
            skLineSegment(sketch, "E307", {"start": v(111.87, 40.99) * mm, "end": v(105.44, 47.41) * mm});
            skLineSegment(sketch, "E308", {"start": v(105.44, 47.41) * mm, "end": v(102.74, 50.12) * mm});
            skLineSegment(sketch, "E309", {"start": v(102.74, 50.12) * mm, "end": v(99.1, 46.77) * mm});
            skLineSegment(sketch, "E310", {"start": v(99.1, 46.77) * mm, "end": v(99.1, 40.99) * mm});
            skArc(sketch, "E311", {"start": v(99.1, 40.99) * mm, "mid": v(94.56, 38.27) * mm, "end": v(92.55, 33.37) * mm});
            skLineSegment(sketch, "E312", {"start": v(92.55, 33.37) * mm, "end": v(92.55, 31.29) * mm});
            skLineSegment(sketch, "E313", {"start": v(92.55, 31.29) * mm, "end": v(89.39, 28.12) * mm});
            skLineSegment(sketch, "E314", {"start": v(89.39, 28.12) * mm, "end": v(87.9, 28.12) * mm});
            skLineSegment(sketch, "E315", {"start": v(87.9, 28.12) * mm, "end": v(87.9, 32.13) * mm});
            skLineSegment(sketch, "E316", {"start": v(87.9, 32.13) * mm, "end": v(79.93, 41.15) * mm});
            skLineSegment(sketch, "E317", {"start": v(-20.85, 25.06) * mm, "end": v(-25.01, 28.43) * mm});
            skLineSegment(sketch, "E318", {"start": v(-25.01, 28.43) * mm, "end": v(-20.85, 33.58) * mm});
            skLineSegment(sketch, "E319", {"start": v(-20.85, 33.58) * mm, "end": v(-13.8, 33.58) * mm});
            skLineSegment(sketch, "E320", {"start": v(-13.8, 33.58) * mm, "end": v(-13.8, 35.33) * mm});
            skLineSegment(sketch, "E321", {"start": v(-13.8, 35.33) * mm, "end": v(-20.85, 45.73) * mm});
            skLineSegment(sketch, "E322", {"start": v(-20.85, 45.73) * mm, "end": v(-11.66, 57.1) * mm});
            skLineSegment(sketch, "E323", {"start": v(-11.66, 57.1) * mm, "end": v(61.9, 45.73) * mm});
            skLineSegment(sketch, "E324", {"start": v(61.9, 45.73) * mm, "end": v(63.5, 44.42) * mm});
            skLineSegment(sketch, "E325", {"start": v(63.5, 44.42) * mm, "end": v(65.7, 47.13) * mm});
            skLineSegment(sketch, "E326", {"start": v(65.7, 47.13) * mm, "end": v(69.66, 42.87) * mm});
            skLineSegment(sketch, "E327", {"start": v(69.66, 42.87) * mm, "end": v(74, 42.87) * mm});
            skLineSegment(sketch, "E328", {"start": v(74, 42.87) * mm, "end": v(79.93, 41.15) * mm});
            skLineSegment(sketch, "E329", {"start": v(-17.01, 30.47) * mm, "end": v(4.78, 13.48) * mm});
            skLineSegment(sketch, "E330", {"start": v(4.78, 13.48) * mm, "end": v(4.78, -4.78) * mm});
            skLineSegment(sketch, "E331", {"start": v(4.78, -4.78) * mm, "end": v(16, -2.22) * mm});
            skLineSegment(sketch, "E332", {"start": v(16, -2.22) * mm, "end": v(12.72, 0) * mm});
            skLineSegment(sketch, "E333", {"start": v(12.72, 0) * mm, "end": v(12.72, 7.29) * mm});
            skLineSegment(sketch, "E334", {"start": v(12.72, 7.29) * mm, "end": v(21.08, 0) * mm});
            skLineSegment(sketch, "E335", {"start": v(21.08, 0) * mm, "end": v(22.21, -2.22) * mm});
            skLineSegment(sketch, "E336", {"start": v(22.21, -2.22) * mm, "end": v(34.04, 0) * mm});
            skLineSegment(sketch, "E337", {"start": v(34.04, 0) * mm, "end": v(12.72, 15.76) * mm});
            skLineSegment(sketch, "E338", {"start": v(12.72, 15.76) * mm, "end": v(12.72, 30.45) * mm});
            skLineSegment(sketch, "E339", {"start": v(12.72, 30.45) * mm, "end": v(0, 30.45) * mm});
            skLineSegment(sketch, "E340", {"start": v(0, 30.45) * mm, "end": v(4.61, 28.93) * mm});
            skLineSegment(sketch, "E341", {"start": v(4.61, 28.93) * mm, "end": v(4.61, 23.54) * mm});
            skLineSegment(sketch, "E342", {"start": v(4.61, 23.54) * mm, "end": v(-2.19, 28.76) * mm});
            skLineSegment(sketch, "E343", {"start": v(-2.19, 28.76) * mm, "end": v(-2.19, 31.46) * mm});
            skLineSegment(sketch, "E344", {"start": v(-2.19, 31.46) * mm, "end": v(-17.01, 30.47) * mm});
            skLineSegment(sketch, "E345", {"start": v(17.72, 30.97) * mm, "end": v(37.05, 15.9) * mm});
            skPoint(sketch, "E345.startSnap0", {"position": v(-9.6, 30.97) * mm});
            skLineSegment(sketch, "E346", {"start": v(37.05, 15.9) * mm, "end": v(38, 1.66) * mm});
            skLineSegment(sketch, "E347", {"start": v(38, 1.66) * mm, "end": v(47.33, 2.29) * mm});
            skLineSegment(sketch, "E348", {"start": v(47.33, 2.29) * mm, "end": v(45.08, 4.04) * mm});
            skLineSegment(sketch, "E349", {"start": v(45.08, 4.04) * mm, "end": v(44.67, 10.23) * mm});
            skLineSegment(sketch, "E350", {"start": v(44.67, 10.23) * mm, "end": v(51.36, 5.01) * mm});
            skLineSegment(sketch, "E351", {"start": v(51.52, 3.87) * mm, "end": v(51.52, 1.66) * mm});
            skLineSegment(sketch, "E352", {"start": v(51.52, 1.66) * mm, "end": v(64.11, 2.5) * mm});
            skLineSegment(sketch, "E353", {"start": v(64.11, 2.5) * mm, "end": v(45.57, 16.96) * mm});
            skLineSegment(sketch, "E354", {"start": v(45.57, 16.96) * mm, "end": v(44.67, 30.37) * mm});
            skLineSegment(sketch, "E355", {"start": v(44.67, 30.37) * mm, "end": v(33.49, 30.37) * mm});
            skLineSegment(sketch, "E356", {"start": v(33.49, 30.37) * mm, "end": v(37.05, 27.6) * mm});
            skLineSegment(sketch, "E357", {"start": v(37.05, 27.6) * mm, "end": v(37.33, 23.54) * mm});
            skLineSegment(sketch, "E358", {"start": v(37.33, 23.54) * mm, "end": v(30.62, 28.76) * mm});
            skLineSegment(sketch, "E359", {"start": v(30.62, 28.76) * mm, "end": v(30.51, 30.47) * mm});
            skLineSegment(sketch, "E360", {"start": v(30.51, 30.47) * mm, "end": v(17.72, 30.97) * mm});
            skLineSegment(sketch, "E361", {"start": v(47.42, 29.03) * mm, "end": v(58.72, 27.8) * mm});
            skLineSegment(sketch, "E362", {"start": v(58.72, 27.8) * mm, "end": v(58.72, 25.26) * mm});
            skLineSegment(sketch, "E363", {"start": v(58.72, 25.26) * mm, "end": v(65.14, 20.57) * mm});
            skLineSegment(sketch, "E364", {"start": v(65.14, 20.57) * mm, "end": v(65.14, 24.65) * mm});
            skLineSegment(sketch, "E365", {"start": v(65.14, 24.65) * mm, "end": v(61.98, 26.68) * mm});
            skLineSegment(sketch, "E366", {"start": v(61.98, 26.68) * mm, "end": v(71.96, 25.66) * mm});
            skLineSegment(sketch, "E367", {"start": v(71.96, 25.66) * mm, "end": v(71.96, 15.17) * mm});
            skLineSegment(sketch, "E368", {"start": v(71.96, 15.17) * mm, "end": v(89.88, 3.15) * mm});
            skLineSegment(sketch, "E369", {"start": v(89.88, 3.15) * mm, "end": v(79.09, 3.15) * mm});
            skLineSegment(sketch, "E370", {"start": v(79.09, 3.15) * mm, "end": v(79.09, 4.58) * mm});
            skLineSegment(sketch, "E371", {"start": v(79.09, 4.58) * mm, "end": v(72.77, 9.06) * mm});
            skLineSegment(sketch, "E372", {"start": v(72.77, 9.06) * mm, "end": v(72.77, 4.27) * mm});
            skLineSegment(sketch, "E373", {"start": v(72.77, 4.27) * mm, "end": v(75.42, 2.74) * mm});
            skLineSegment(sketch, "E374", {"start": v(75.42, 2.74) * mm, "end": v(66.15, 2.95) * mm});
            skLineSegment(sketch, "E375", {"start": v(66.15, 2.95) * mm, "end": v(66.15, 14.36) * mm});
            skLineSegment(sketch, "E376", {"start": v(66.15, 14.36) * mm, "end": v(47.42, 29.03) * mm});
            skLineSegment(sketch, "E377", {"start": v(72.97, 25.61) * mm, "end": v(102.6, 1.47) * mm});
            skLineSegment(sketch, "E378", {"start": v(102.6, 1.47) * mm, "end": v(97.6, 21.33) * mm});
            skLineSegment(sketch, "E379", {"start": v(97.6, 21.33) * mm, "end": v(88.24, 23.06) * mm});
            skLineSegment(sketch, "E380", {"start": v(88.24, 23.06) * mm, "end": v(92.21, 20) * mm});
            skLineSegment(sketch, "E381", {"start": v(92.21, 20) * mm, "end": v(93.84, 13.39) * mm});
            skLineSegment(sketch, "E382", {"start": v(93.84, 13.39) * mm, "end": v(84.27, 21.13) * mm});
            skLineSegment(sketch, "E383", {"start": v(84.27, 21.13) * mm, "end": v(84.27, 23.57) * mm});
            skLineSegment(sketch, "E384", {"start": v(84.27, 23.57) * mm, "end": v(72.97, 25.61) * mm});
            skLineSegment(sketch, "E385", {"start": v(114.85, 0) * mm, "end": v(126.15, -0.98) * mm});
            skLineSegment(sketch, "E386", {"start": v(114.85, 0) * mm, "end": v(114.85, 3.42) * mm});
            skLineSegment(sketch, "E387", {"start": v(114.85, 3.42) * mm, "end": v(104.3, 16.53) * mm});
            skLineSegment(sketch, "E388", {"start": v(104.3, 16.53) * mm, "end": v(99.07, 20) * mm});
            skLineSegment(sketch, "E389", {"start": v(99.07, 20) * mm, "end": v(111.7, 17.02) * mm});
            skLineSegment(sketch, "E390", {"start": v(111.7, 17.02) * mm, "end": v(111.7, 15.05) * mm});
            skLineSegment(sketch, "E391", {"start": v(111.7, 15.05) * mm, "end": v(122.72, 1.47) * mm});
            skLineSegment(sketch, "E392", {"start": v(122.72, 1.47) * mm, "end": v(126.15, -0.98) * mm});
            skLineSegment(sketch, "E393", {"start": v(128.24, 0.67) * mm, "end": v(128.95, 0) * mm});
            skLineSegment(sketch, "E394", {"start": v(51.36, 5.01) * mm, "end": v(51.52, 3.87) * mm});
            skSolve(sketch);
        }
        {
            var Q0;
            Q0 = qSketchRegion(id + "F8", true);
            extrude(context, id + "F9", {"entities" : qUnion([Q0]), "operationType" : NewBodyOperationType.ADD, "depth" : 12.7 * mm});
        }
        {
            var Q0;
            Q0=makeQuery(id+"F6.imprint","IMPRINT",FACE,{"disambiguationData":[TD([[makeQuery(id+"F6.imprint","IMPRINT",EDGE,{"derivedFrom":sQuery(id+"F6.wireOp",EDGE,"E186")}),1.0]])]});
            var sketch = newSketch(context, id + "F10", { "sketchPlane" : qUnion([Q0])});
            skText(sketch, "E395", { "text": "Super Bowl 36\nPatriots 20 St.Louis Rams 17", "fontName": "OpenSans-Regular.ttf"});
            skText(sketch, "E396", { "text": "Super Bowl38\nPatriots 32 Panthers 29", "fontName": "OpenSans-Regular.ttf"});
            skText(sketch, "E397", { "text": "Super Bowl 39\nPatriots 24 Eagles 21", "fontName": "OpenSans-Regular.ttf"});
            skText(sketch, "E398", { "text": "Super Bowl 49\nPatriots 28 Seahawks 24", "fontName": "OpenSans-Regular.ttf"});
            const initialGuessF10  = {"E395": [-0.02515, -0.06092, 1, 0, 0.01087], "E396": [0.28036, -0.0484, 1, 0, 0.00924], "E397": [-0.02587, -0.10735, 1, 0, 0.00853], "E398": [0.286, -0.07939, 1, 0, 0.00707]};
            skSetInitialGuess(sketch, initialGuessF10);
            skSolve(sketch);
        }
        {
            var Q0;
            Q0 = qSketchRegion(id + "F10", true);
            extrude(context, id + "F11", {"entities" : qUnion([Q0]), "operationType" : NewBodyOperationType.ADD, "depth" : 6.35 * mm});
        }
    });
